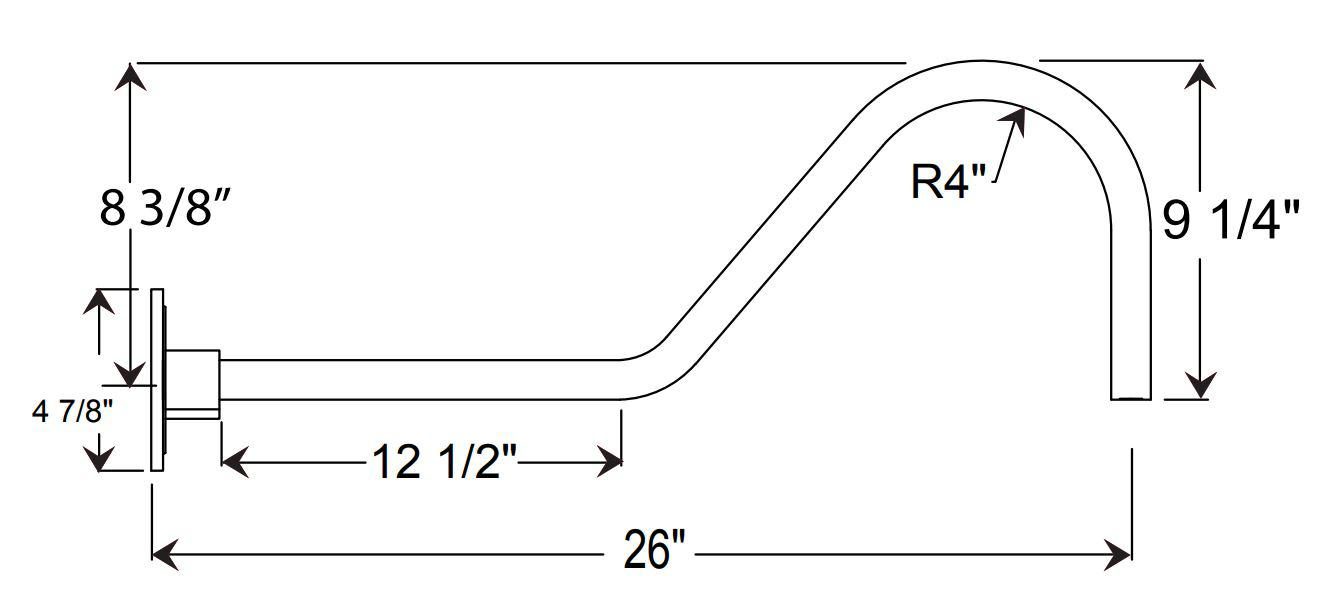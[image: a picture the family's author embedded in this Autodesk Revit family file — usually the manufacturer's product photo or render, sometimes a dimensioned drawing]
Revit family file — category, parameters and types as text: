
# Revit family: Magnolia(12,16,20,24) MB
name_source: partatom
category: Lighting Fixtures
units: mm (PartAtom-declared; Revit-internal decimal feet)

## family parameters
Always vertical = Yes
Cut with Voids When Loaded = No
Light Source = Yes
OmniClass Number = 23.80.70.00
OmniClass Title = Lighting
Part Type = Normal
Room Calculation Point = No
Round Connector Dimension = Use Diameter
Shared = No
Work Plane-Based = No

## types (4) — shared parameters
Apparent Load = 60 VA
Body Colour = Spun aluminium
Body Material = body
CRI = >90
Color Filter = 16777215
Construction Material = Heavy Duty spun aluminum.
Default Elevation = 0' - 0"
Description = 120-277 Voltage
Dimming = 1%
Dimming Lamp Color Temperature Shift = <None>
Efficiency = 65-125 lumens per watt
Fixture Finish = Fixture Finish
INSIDE BODY = INSIDE BODY
Lamp = MB
Life = L70 50,000 hours
Load Classification = Lighting
Manufacturer = ANP Lighting
Power Factor = 1
Tilt Angle = 90.00°
URL = https://www.anplighting.com
Voltage = 277 V
Warranty = 5 year limited warranty
Wattage Comments = 60W Max

## per-type parameters (varying)
| type | Fixture Diameter | Fixture Height | MDM12 | MDM16 | MDM20 | MDM24 | Photometric Web File | Weight |
| MDM12 | 1' - 0" | 1' - 0" | Yes | No | No | No | MDM12M010LD35K.IES | 4.5lbs |
| MDM16 | 1' - 4" | 1' - 4" | No | Yes | No | No | MDM16M016LD35K.IES | 5.0lbs |
| MDM20 | 1' - 8" | 1' - 8" | No | No | Yes | No | MDM20M016LD35K.IES | 5.5bs |
| MDM24 | 2' - 0" | 2' - 0" | No | No | No | Yes | MDM24M024LD35K.IES | 6.0bs |

note: column(s) folded — value = type name in every type: Model

## geometry (parser evidence)
native form markers: Sweep x21
no freeform markers — native parametric forms only
